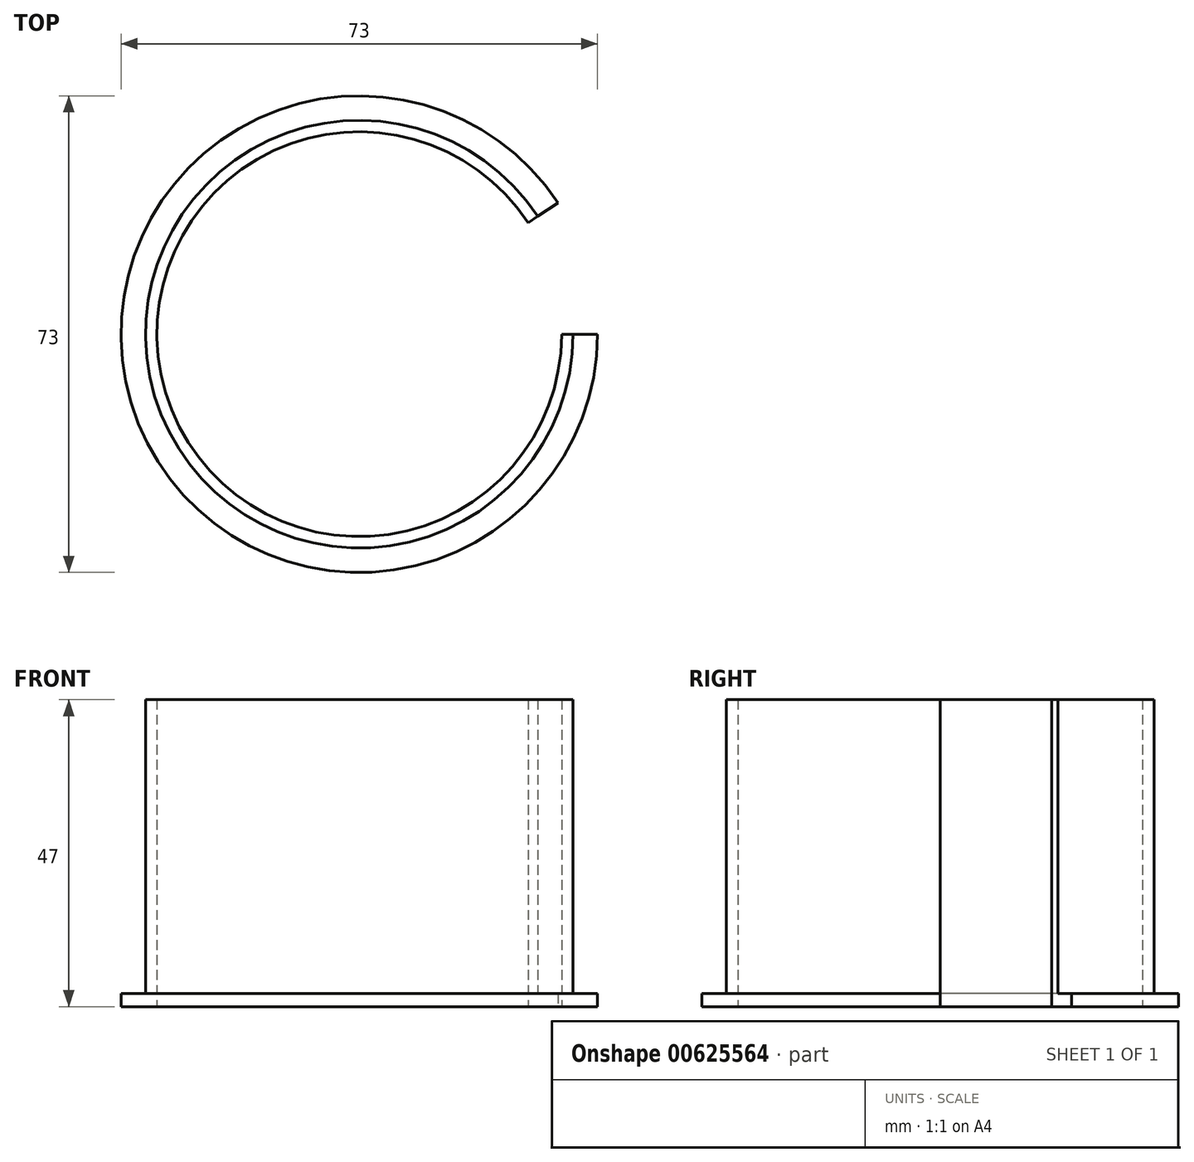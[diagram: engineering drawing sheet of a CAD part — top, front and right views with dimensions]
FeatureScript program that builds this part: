
annotation { "Feature Type Name" : "Feature", "Feature Type Description" : "" }
export const myFeature = defineFeature(function(context is Context, id is Id, definition is map)
    precondition{}
    {
        {
            var Q0;
            Q0=qCreatedBy(makeId("Top.planeOp"),FACE);
            var sketch = newSketch(context, id + "F0", { "sketchPlane" : qUnion([Q0])});
            skCircle(sketch, "E0", {"center": v(0, 0) * mm, "radius": 31 * mm});
            skCircle(sketch, "E1", {"center": v(0, 0) * mm, "radius": 32.75 * mm});
            skSolve(sketch);
        }
        {
            var Q0;
            Q0 = qSketchRegion(id + "F0", true);
            extrude(context, id + "F1", {"entities" : qUnion([Q0]), "depth" : 47 * mm, "offsetDistance" : 25 * mm});
        }
        {
            var Q0;
            Q0=qCreatedBy(makeId("Top.planeOp"),FACE);
            var sketch = newSketch(context, id + "F2", { "sketchPlane" : qUnion([Q0])});
            skCircle(sketch, "E2", {"center": v(0, 0) * mm, "radius": 36.5 * mm});
            skCircle(sketch, "E3", {"center": v(0, 0) * mm, "radius": 31 * mm});
            skSolve(sketch);
        }
        {
            var Q0;
            Q0 = qSketchRegion(id + "F2", true);
            extrude(context, id + "F3", {"entities" : qUnion([Q0]), "operationType" : NewBodyOperationType.ADD, "depth" : 2 * mm, "offsetDistance" : 25 * mm});
        }
        {
            var Q0;
            Q0=qCreatedBy(makeId("Top.planeOp"),FACE);
            var sketch = newSketch(context, id + "F4", { "sketchPlane" : qUnion([Q0])});
            skLineSegment(sketch, "E4", {"start": v(0, 0) * mm, "end": v(36.5, 0) * mm, "construction": true});
            skLineSegment(sketch, "E5", {"start": v(0, 0) * mm, "end": v(30.46, 20.11) * mm, "construction": true});
            skLineSegment(sketch, "E6", {"start": v(30.46, 20.11) * mm, "end": v(25.87, 17.08) * mm});
            skLineSegment(sketch, "E7", {"start": v(36.5, 0) * mm, "end": v(31, 0) * mm});
            skArc(sketch, "E8", {"start": v(36.5, 0) * mm, "mid": v(34.96, 10.5) * mm, "end": v(30.46, 20.11) * mm});
            skArc(sketch, "E9", {"start": v(31, 0) * mm, "mid": v(29.69, 8.92) * mm, "end": v(25.87, 17.08) * mm});
            skSolve(sketch);
        }
        {
            var Q0;
            Q0 = qSketchRegion(id + "F4", true);
            extrude(context, id + "F5", {"entities" : qUnion([Q0]), "operationType" : NewBodyOperationType.REMOVE, "endBound" : BoundingType.UP_TO_NEXT, "depth" : 25 * mm, "offsetDistance" : 25 * mm});
        }
    });
